# Revit family: HL_RU_Roof drain_HL64PPowerSafe-B-221103
name_source: partatom
category: Instalační zařizovací předměty
units: mm (PartAtom-declared; Revit-internal decimal feet)

## family parameters
Bod výpočtu místnosti = Ano
Kóta kulaté spojky = Použít průměr
Nadpis OmniClass = Deck Waste Water Drains
Ořezat dutým tvarem při načtení = Ne
Sdílené = Ne
Typ dílu = Normální
Vždy vertikální = Ano
Založené na pracovní rovině = Ne
Číslo OmniClass = 23.70.50.21.24.14

## types (1)
- HL_Кровельная воронка_HL64PPowerSafe
    EAN = 9003076040889
    Indexovaná poznámka = HL64PPowerSafe
    Komentáře k typům = HL64PPowerSafe, Воронка для аварийного водостока с отсекателем воздуха, с горизонтальным выпуском DN75, с корпусом из ПВХ, с возможностью регулировки толщины слоя воды.
    Model = HL64PPowerSafe
    Popis = Кровельные воронки
    Přípoj CW = Ne
    Přípoj HW = Ne
    Přípoj odpadních dílů = Ano
    Přípoj ventilace = Ne
    URL = http://www.hutterer-lechner.com
    Výchozí výška = 0 mm  [stored 0 ft]
    Výrobce = HL Hutterer & Lechner GmbH
    ВЕС = 3,284 [kg]
    ВЫСОТА МОНТАЖА = 93 mm
    МАТЕРИАЛ = PP/PVC
    НОМИНАЛЬНЫЙ ДИАМЕТР = 75 mm
    РАЗМЕР = DN75
    РЕШЁТКА = Laubfangkorb d 262 mm

note: [stored X ft] marks values corroborated as IEEE doubles in the binary element streams (Revit-internal decimal feet)

## geometry (parser evidence)
native form markers: Sweep x3
no freeform markers — native parametric forms only
